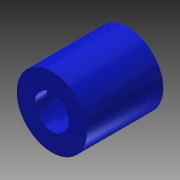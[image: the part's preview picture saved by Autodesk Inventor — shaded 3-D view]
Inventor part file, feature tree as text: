
AUTODESK INVENTOR PART (.ipt)
format: ipt  version: 2014 (Build 180170000, 170)  size: 111,104 bytes
history: native  units: in
note: dims shown in document units (in); Inventor stores cm internally (conversion verified against a paired STEP export)
features: extrude x4, sketch x4
ambient origin geometry x8: Origin, YZ Plane, XZ Plane, XY Plane, X Axis, Y Axis, Z Axis, Center Point
bodies: Solid1 (feature_tree)
feature tree (8):
  extrude  "Extrusion1"  Depth=0.25in TaperAngle=0.0deg
  extrude  "Extrusion2"  Depth=0.247in TaperAngle=0.0deg
  extrude  "Extrusion4"  Depth=0.27in TaperAngle=0.0deg
  extrude  "Extrusion5"  Depth=0.1385in TaperAngle=0.0deg
  sketch  "Sketch1"  dims[d0=0.6325in d1=0.25in d2=0.0in]
  sketch  "Sketch3"  dims[d3=0.1in d5=0.247in d6=0.0in]
  sketch  "Sketch7"  dims[d12=0.5975in d13=0.27in d14=0.0in]
  sketch  "Sketch8"  dims[d15=0.4005in d16=0.1385in d17=0.0in]
